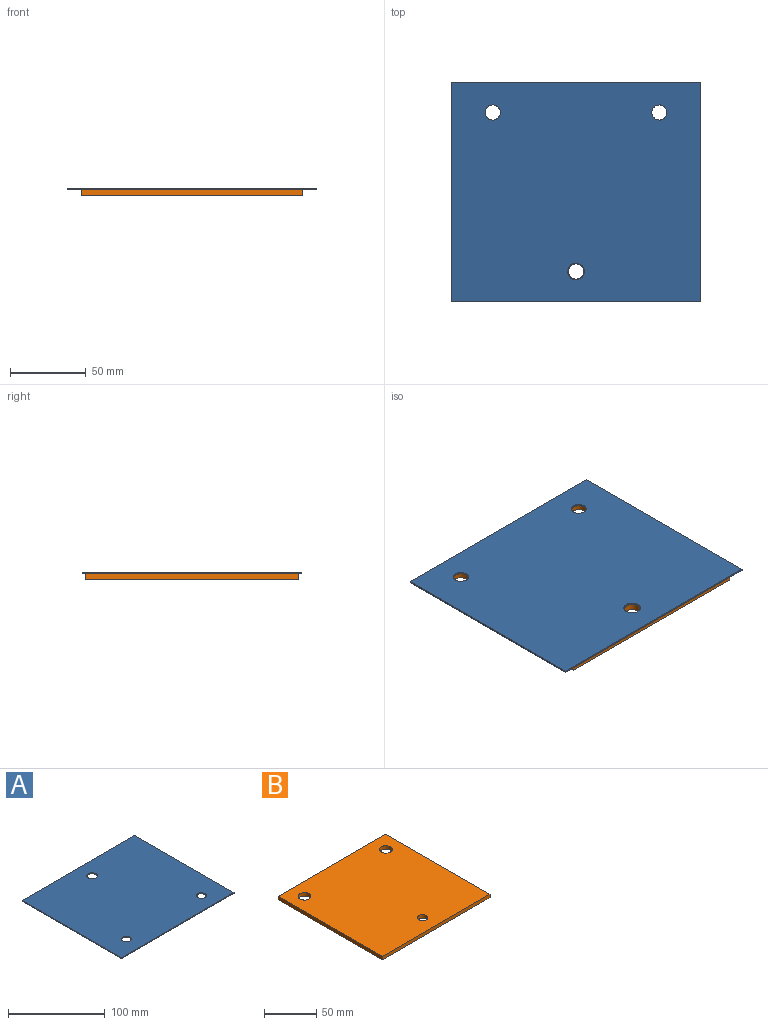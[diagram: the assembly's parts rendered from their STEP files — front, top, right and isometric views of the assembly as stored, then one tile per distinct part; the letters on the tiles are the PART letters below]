
ASSEMBLY  parts=2 mates=1
PART A: 9 faces, bbox 165x145x1 mm
  f0: plane 165x1mm, normal (0,-1,0), area 165mm2, adj f1,f5,f7,f8
  f1: plane 145x1mm, normal (1,0,0), area 145mm2, adj f0,f2,f7,f8
  f2: plane 165x1mm, normal (0,1,0), area 165mm2, adj f1,f5,f7,f8
  f3: cylinder r=5mm len=10mm, axis (0,0,-1), area 31.4mm2, adj f7,f8
  f4: cylinder r=5mm len=10mm, axis (0,0,-1), area 31.4mm2, adj f7,f8
  f5: plane 145x1mm, normal (-1,0,0), area 145mm2, adj f0,f2,f7,f8
  f6: cylinder r=5.5mm len=11mm, axis (0,0,-1), area 34.6mm2, adj f7,f8
  f7: plane 165x145mm, normal (0,0,1), area 23672.9mm2, adj f0,f1,f2,f3,f4,f5,f6
  f8: plane 165x145mm, normal (0,0,-1), area 23672.9mm2, adj f0,f1,f2,f3,f4,f5,f6
PART B: 9 faces, bbox 146x141x4 mm
  f0: plane 141x4mm, normal (1,0,0), area 564mm2, adj f1,f5,f7,f8
  f1: plane 146x4mm, normal (0,1,0), area 584mm2, adj f0,f2,f7,f8
  f2: plane 141x4mm, normal (-1,0,0), area 564mm2, adj f1,f5,f7,f8
  f3: cylinder r=5mm len=10mm, axis (0,0,-1), area 125.7mm2, adj f7,f8
  f4: cylinder r=6.1mm len=12.2mm, axis (0,0,-1), area 153.3mm2, adj f7,f8
  f5: plane 146x4mm, normal (0,-1,0), area 584mm2, adj f0,f2,f7,f8
  f6: cylinder r=6.1mm len=12.2mm, axis (0,0,-1), area 153.3mm2, adj f7,f8
  f7: plane 146x141mm, normal (0,0,1), area 20273.7mm2, adj f0,f1,f2,f3,f4,f5,f6
  f8: plane 146x141mm, normal (0,0,-1), area 20273.7mm2, adj f0,f1,f2,f3,f4,f5,f6
PLACE A rot(axis=(1,0,0),180deg) t=(-56.53,-23.75,16.32)mm
PLACE B t=(-56.53,-23.75,11.32)mm
MATE revolute A.f6 <-> B.f3  axis (0,0,-1) through (-56.53,-76.25,15.32)mm
